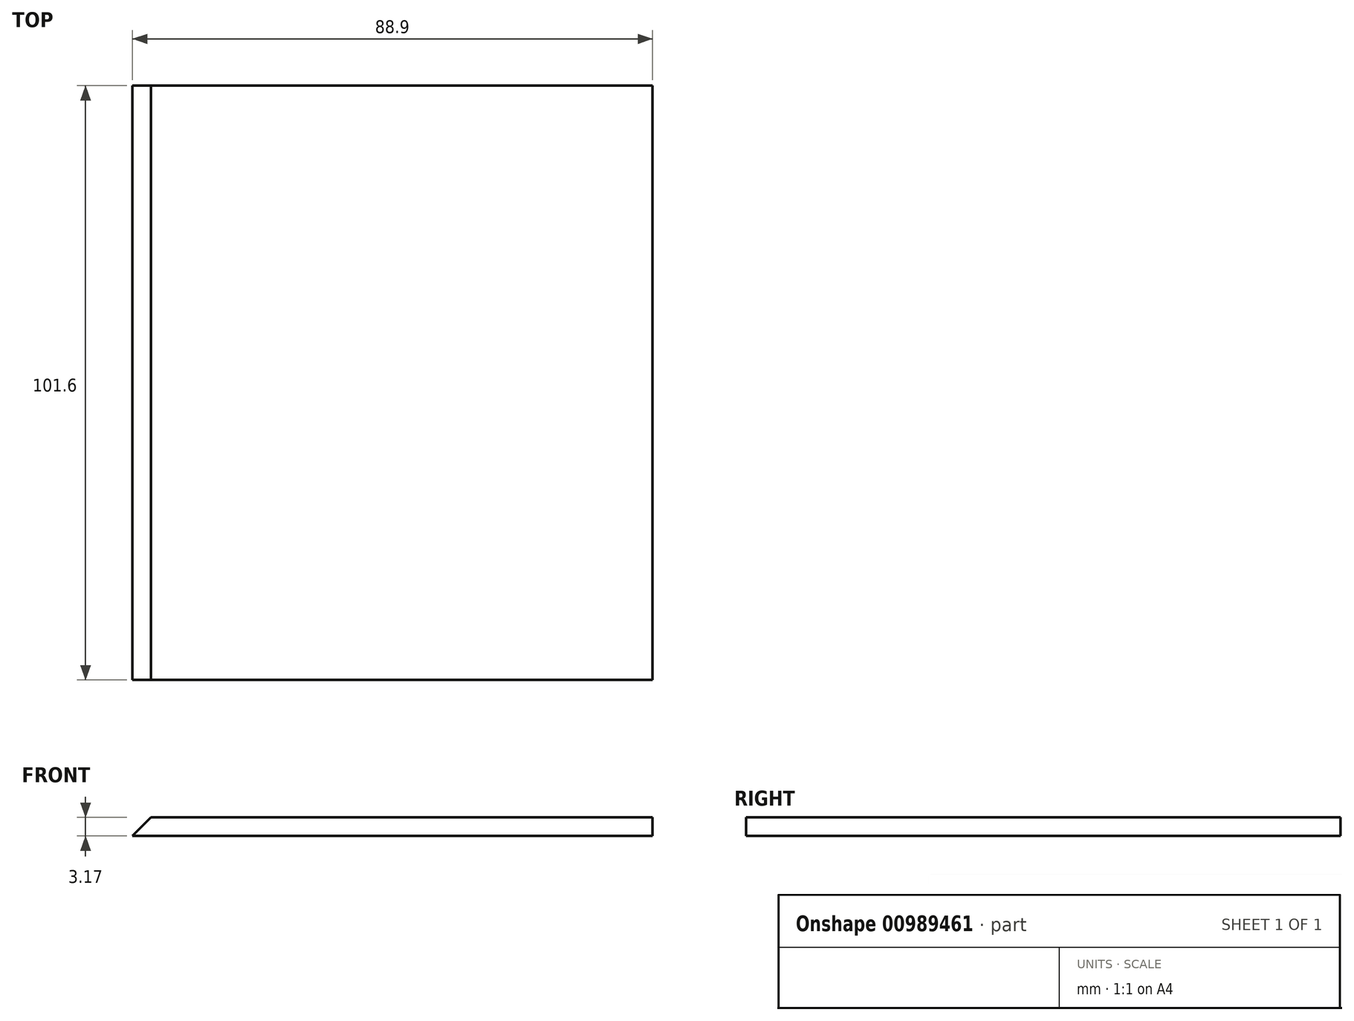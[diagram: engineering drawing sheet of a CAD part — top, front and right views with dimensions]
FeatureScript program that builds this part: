
annotation { "Feature Type Name" : "Feature", "Feature Type Description" : "" }
export const myFeature = defineFeature(function(context is Context, id is Id, definition is map)
    precondition{}
    {
        {
            var Q0;
            Q0=qCreatedBy(makeId("Front.planeOp"),FACE);
            var sketch = newSketch(context, id + "F0", { "sketchPlane" : qUnion([Q0])});
            skLineSegment(sketch, "E0.bottom", {"start": v(56.62, 1.32) * mm, "end": v(-29.1, 1.32) * mm});
            skLineSegment(sketch, "E0.top", {"start": v(56.62, -1.85) * mm, "end": v(-32.28, -1.85) * mm});
            skLineSegment(sketch, "E0.left", {"start": v(56.62, 1.32) * mm, "end": v(56.62, -1.85) * mm});
            skPoint(sketch, "E0.middle", {"position": v(12.17, -0.26) * mm});
            skLineSegment(sketch, "E1", {"start": v(-32.28, -1.85) * mm, "end": v(-29.1, 1.32) * mm});
            skPoint(sketch, "E2.orphan", {"position": v(-32.28, 1.32) * mm});
            skSolve(sketch);
        }
        {
            var Q0;
            Q0=makeQuery(id+"F0.imprint","IMPRINT",FACE,{"disambiguationData":[TD([[makeQuery(id+"F0.imprint","IMPRINT",EDGE,{"derivedFrom":sQuery(id+"F0.wireOp",EDGE,"E0.bottom")}),1.0]])]});
            extrude(context, id + "F1", {"entities" : qUnion([Q0]), "endBound" : BoundingType.SYMMETRIC, "depth" : 101.6 * mm, "offsetDistance" : 25.4 * mm});
        }
    });
